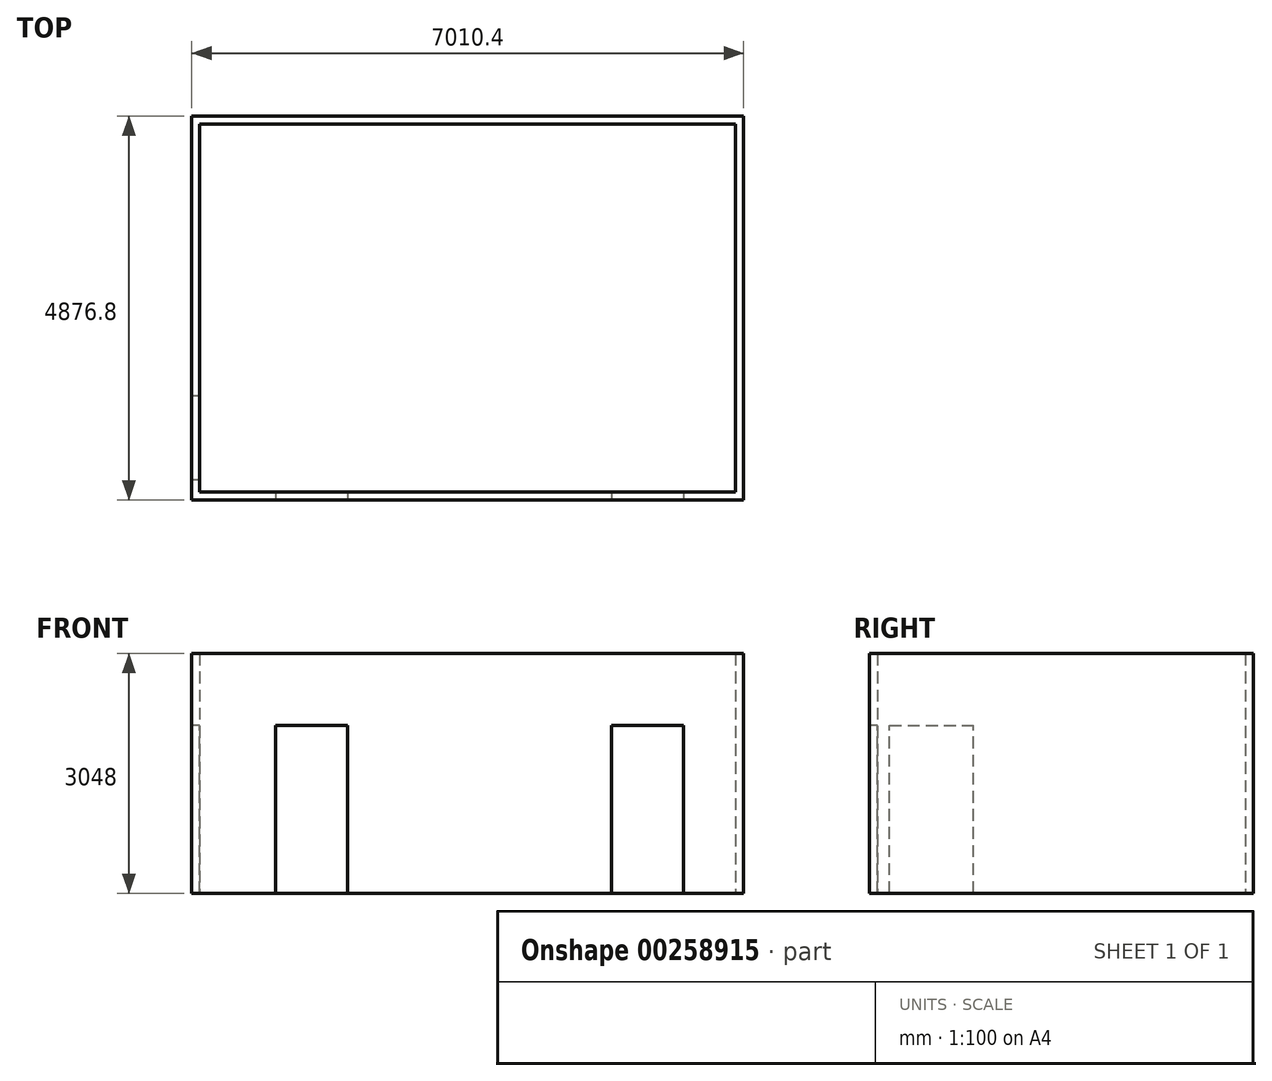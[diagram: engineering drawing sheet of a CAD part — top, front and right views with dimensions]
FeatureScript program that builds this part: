
annotation { "Feature Type Name" : "Feature", "Feature Type Description" : "" }
export const myFeature = defineFeature(function(context is Context, id is Id, definition is map)
    precondition{}
    {
        {
            var Q0;
            Q0=qCreatedBy(makeId("Top.planeOp"),FACE);
            var sketch = newSketch(context, id + "F0", { "sketchPlane" : qUnion([Q0])});
            skLineSegment(sketch, "E0.bottom", {"start": v(3505.2, 2438.4) * mm, "end": v(-3505.2, 2438.4) * mm});
            skLineSegment(sketch, "E0.top", {"start": v(3505.2, -2438.4) * mm, "end": v(-3505.2, -2438.4) * mm});
            skLineSegment(sketch, "E0.left", {"start": v(3505.2, 2438.4) * mm, "end": v(3505.2, -2438.4) * mm});
            skLineSegment(sketch, "E0.right", {"start": v(-3505.2, 2438.4) * mm, "end": v(-3505.2, -2438.4) * mm});
            skPoint(sketch, "E0.middle", {"position": v(0, 0) * mm});
            skSolve(sketch);
        }
        {
            var Q0;
            Q0=makeQuery(id+"F0.imprint","IMPRINT",FACE,{"disambiguationData":[TD([[makeQuery(id+"F0.imprint","IMPRINT",EDGE,{"derivedFrom":sQuery(id+"F0.wireOp",EDGE,"E0.bottom")}),1.0]])]});
            extrude(context, id + "F1", {"entities" : qUnion([Q0]), "depth" : 3048 * mm});
        }
        {
            var Q0;
            Q0=makeQuery(id+"F1.opExtrude","CAP_FACE",FACE,{"disambiguationData":[OSD([sQuery(id+"F0.wireOp",EDGE,"E0.bottom"),sQuery(id+"F0.wireOp",EDGE,"E0.top"),sQuery(id+"F0.wireOp",EDGE,"E0.left"),sQuery(id+"F0.wireOp",EDGE,"E0.right")])],"isStart":false});
            shell(context, id + "F2", {"entities" : qUnion([Q0]), "thickness" : 101.6 * mm});
        }
        {
            var Q0;
            Q0=makeQuery(id+"F1.opExtrude","SWEPT_FACE",FACE,{"disambiguationData":[OSD([sQuery(id+"F0.wireOp",EDGE,"E0.top")])]});
            var sketch = newSketch(context, id + "F3", { "sketchPlane" : qUnion([Q0])});
            skLineSegment(sketch, "E1.bottom", {"start": v(-2438.4, 2.54) * mm, "end": v(-1524, 2.54) * mm});
            skLineSegment(sketch, "E1.top", {"start": v(-2438.4, 2136.14) * mm, "end": v(-1524, 2136.14) * mm});
            skLineSegment(sketch, "E1.left", {"start": v(-2438.4, 2.54) * mm, "end": v(-2438.4, 2136.14) * mm});
            skLineSegment(sketch, "E1.right", {"start": v(-1524, 2.54) * mm, "end": v(-1524, 2136.14) * mm});
            skLineSegment(sketch, "E2.bottom", {"start": v(1828.8, 2.54) * mm, "end": v(2743.2, 2.54) * mm});
            skLineSegment(sketch, "E2.top", {"start": v(1828.8, 2136.14) * mm, "end": v(2743.2, 2136.14) * mm});
            skLineSegment(sketch, "E2.left", {"start": v(1828.8, 2.54) * mm, "end": v(1828.8, 2136.14) * mm});
            skLineSegment(sketch, "E2.right", {"start": v(2743.2, 2.54) * mm, "end": v(2743.2, 2136.14) * mm});
            skSolve(sketch);
        }
        {
            var Q0;
            Q0=makeQuery(id+"F3.imprint","IMPRINT",FACE,{"disambiguationData":[TD([[makeQuery(id+"F3.imprint","IMPRINT",EDGE,{"derivedFrom":sQuery(id+"F3.wireOp",EDGE,"E1.bottom")}),1.0]])]});
            var Q1;
            Q1=makeQuery(id+"F3.imprint","IMPRINT",FACE,{"disambiguationData":[TD([[makeQuery(id+"F3.imprint","IMPRINT",EDGE,{"derivedFrom":sQuery(id+"F3.wireOp",EDGE,"E2.bottom")}),1.0]])]});
            extrude(context, id + "F4", {"entities" : qUnion([Q0, Q1]), "operationType" : NewBodyOperationType.REMOVE, "oppositeDirection" : true, "depth" : 101.6 * mm});
        }
        {
            var Q0;
            Q0=makeQuery(id+"F2.opShell","OFFSET_FACE",FACE,{"disambiguationData":[OSD([sQuery(id+"F0.wireOp",EDGE,"E0.bottom"),sQuery(id+"F0.wireOp",EDGE,"E0.top"),sQuery(id+"F0.wireOp",EDGE,"E0.left"),sQuery(id+"F0.wireOp",EDGE,"E0.right")])]});
            extrude(context, id + "F5", {"entities" : qUnion([Q0]), "operationType" : NewBodyOperationType.REMOVE, "oppositeDirection" : true, "depth" : 99.06 * mm});
        }
        {
            var Q0;
            Q0=makeQuery(id+"F1.opExtrude","SWEPT_FACE",FACE,{"disambiguationData":[OSD([sQuery(id+"F0.wireOp",EDGE,"E0.right")])]});
            var sketch = newSketch(context, id + "F6", { "sketchPlane" : qUnion([Q0])});
            skLineSegment(sketch, "E3.bottom", {"start": v(2184.4, 2.54) * mm, "end": v(1117.6, 2.54) * mm});
            skLineSegment(sketch, "E3.top", {"start": v(2184.4, 2136.14) * mm, "end": v(1117.6, 2136.14) * mm});
            skLineSegment(sketch, "E3.left", {"start": v(2184.4, 2.54) * mm, "end": v(2184.4, 2136.14) * mm});
            skLineSegment(sketch, "E3.right", {"start": v(1117.6, 2.54) * mm, "end": v(1117.6, 2136.14) * mm});
            skSolve(sketch);
        }
        {
            var Q0;
            Q0=makeQuery(id+"F6.imprint","IMPRINT",FACE,{"disambiguationData":[TD([[makeQuery(id+"F6.imprint","IMPRINT",EDGE,{"derivedFrom":sQuery(id+"F6.wireOp",EDGE,"E3.bottom")}),-1.0]])]});
            extrude(context, id + "F7", {"entities" : qUnion([Q0]), "operationType" : NewBodyOperationType.REMOVE, "oppositeDirection" : true, "depth" : 101.6 * mm});
        }
    });
